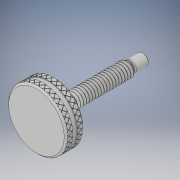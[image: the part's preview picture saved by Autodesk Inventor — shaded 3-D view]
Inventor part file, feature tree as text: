
AUTODESK INVENTOR PART (.ipt)
format: ipt  version: 2019 (Build 230136000, 136)  size: 2,498,048 bytes
history: native  units: in
note: dims shown in document units (in); Inventor stores cm internally (conversion verified against a paired STEP export)
features: chamfer x1, other x1
ambient origin geometry x8: Origin, YZ Plane, XZ Plane, XY Plane, X Axis, Y Axis, Z Axis, Center Point
bodies: Solid1 (feature_tree), Solid2 (feature_tree)
feature tree (2):
  chamfer  "Chamfer4"  [1 undecoded]
  other  "Cut-Revolve2"
note: 1 required parameter value undecoded (feature->parameter linkage not recoverable at this tier; creation-order binding heuristic only, values carry confidence <= 0.55)
